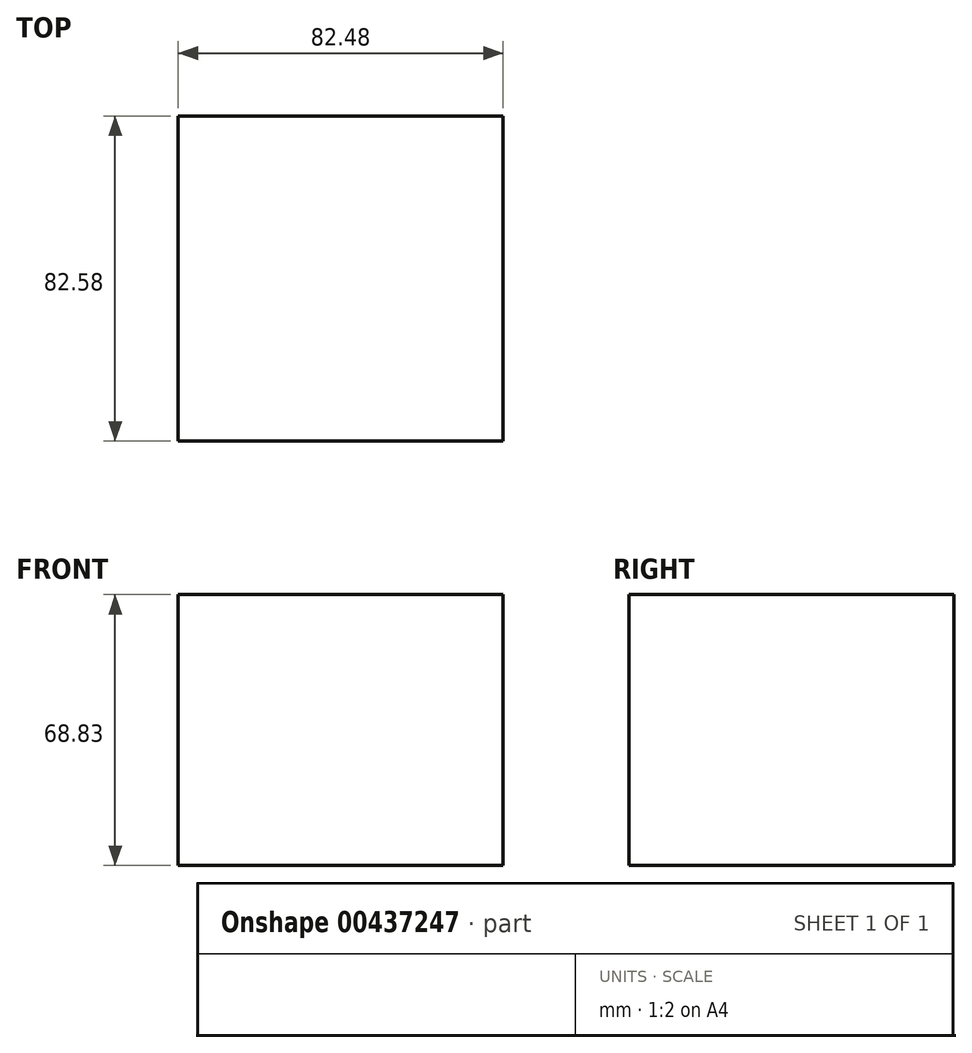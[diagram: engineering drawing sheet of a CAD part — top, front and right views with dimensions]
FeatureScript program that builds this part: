
annotation { "Feature Type Name" : "Feature", "Feature Type Description" : "" }
export const myFeature = defineFeature(function(context is Context, id is Id, definition is map)
    precondition{}
    {
        {
            var Q0;
            Q0=qCreatedBy(makeId("Top.planeOp"),FACE);
            var sketch = newSketch(context, id + "F0", { "sketchPlane" : qUnion([Q0])});
            skLineSegment(sketch, "E0.bottom", {"start": v(-41.24, -41.3) * mm, "end": v(41.24, -41.3) * mm});
            skLineSegment(sketch, "E0.top", {"start": v(-41.24, 41.3) * mm, "end": v(41.24, 41.3) * mm});
            skLineSegment(sketch, "E0.left", {"start": v(-41.24, -41.3) * mm, "end": v(-41.24, 41.3) * mm});
            skLineSegment(sketch, "E0.right", {"start": v(41.24, -41.3) * mm, "end": v(41.24, 41.3) * mm});
            skPoint(sketch, "E0.middle", {"position": v(0, 0) * mm});
            skSolve(sketch);
        }
        {
            var Q0;
            Q0=makeQuery(id+"F0.imprint","IMPRINT",FACE,{"disambiguationData":[TD([[makeQuery(id+"F0.imprint","IMPRINT",EDGE,{"derivedFrom":sQuery(id+"F0.wireOp",EDGE,"E0.bottom")}),1.0]])]});
            extrude(context, id + "F1", {"entities" : qUnion([Q0]), "depth" : 68.83 * mm});
        }
    });
